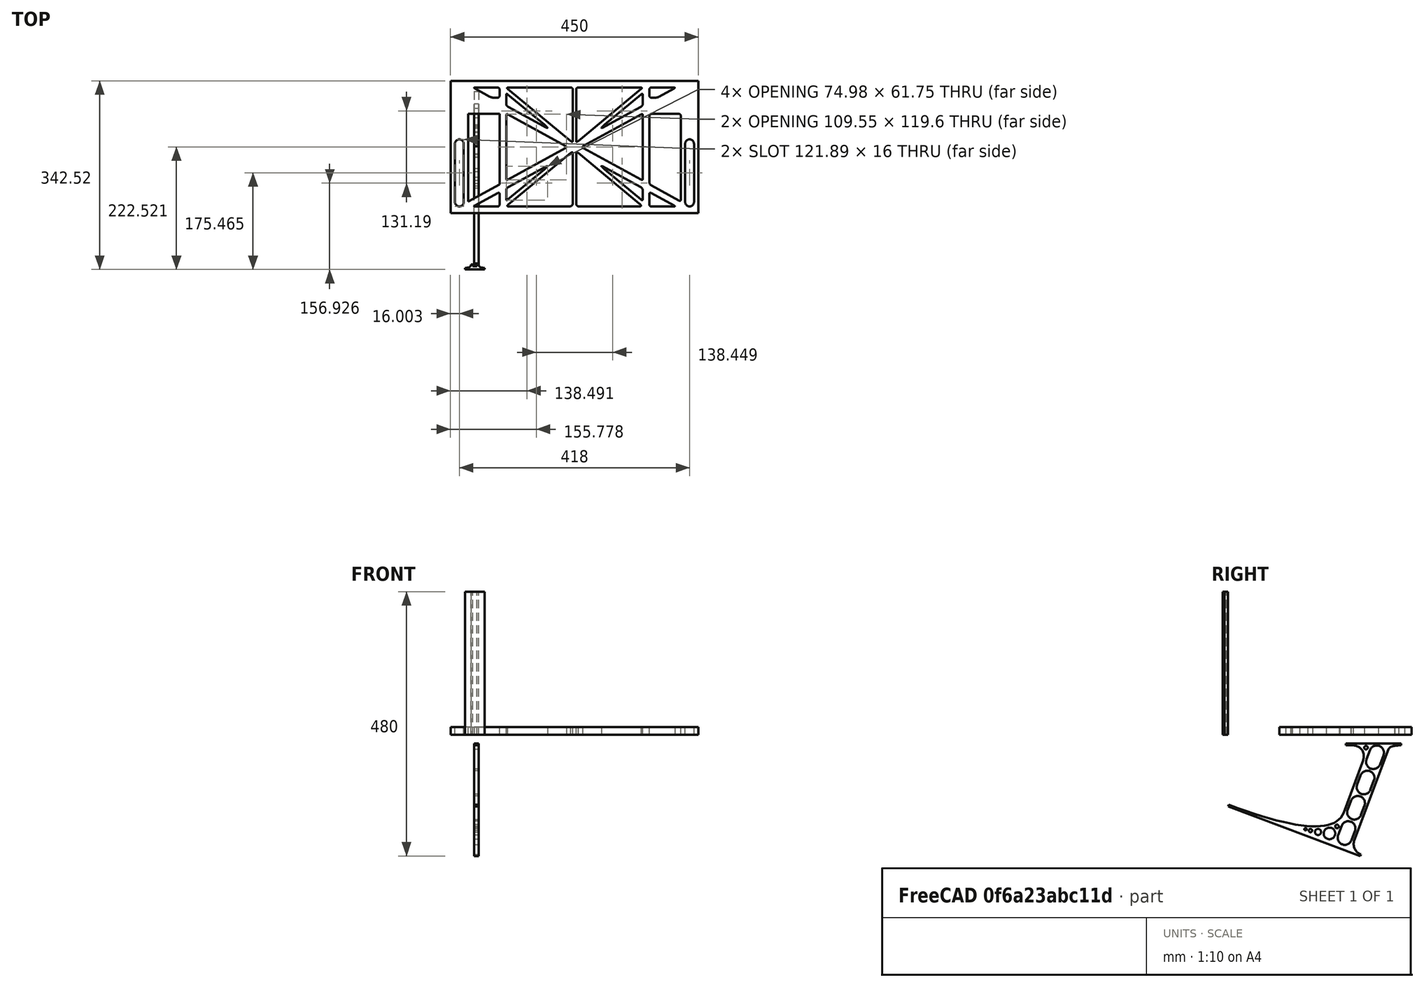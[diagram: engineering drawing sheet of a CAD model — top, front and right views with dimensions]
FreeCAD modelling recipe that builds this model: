
FCSTD DOCUMENT  (FreeCAD 0.19R0.19.2)
Label: laptopStand134FCStd
License: All rights reserved
LicenseURL: http://en.wikipedia.org/wiki/All_rights_reserved
objects: Sketcher::SketchObject×3, Part::Extrusion×3
note: 6 computed .brp shape members not serialized (recipe doc carries the construction recipe); baked Part::Feature solids carry a one-line shape summary decoded from their .brp

FEATURE [Sketcher::SketchObject] Sketch
  FullyConstrained = true
  sketch-geometry (349):
    g0: LineSegment StartX=-10.9272 StartY=-82.7794 StartZ=0 EndX=46.0728 EndY=-51.4823 EndZ=0
    g1: LineSegment StartX=-10.9272 StartY=76.4095 StartZ=0 EndX=-10.9272 EndY=-82.7794 EndZ=0
    g2: LineSegment StartX=46.0728 StartY=76.4095 StartZ=0 EndX=46.0728 EndY=-51.4823 EndZ=0
    g3: LineSegment StartX=-42.9272 StartY=136.221 StartZ=0 EndX=-42.9272 EndY=-103.779 EndZ=0
    g4: LineSegment StartX=407.073 StartY=136.221 StartZ=0 EndX=407.073 EndY=-103.779 EndZ=0
    g5: ArcOfCircle CenterX=-26.9272 CenterY=22.1087 CenterZ=0 NormalX=0 NormalY=0 NormalZ=1 AngleXU=0 Radius=8 StartAngle=1e-16 EndAngle=3.14159
    g6: ArcOfCircle CenterX=-26.9272 CenterY=-83.7794 CenterZ=0 NormalX=0 NormalY=0 NormalZ=1 AngleXU=0 Radius=8 StartAngle=3.14159 EndAngle=6.28319
    g7: LineSegment StartX=-34.9272 StartY=22.1087 StartZ=0 EndX=-34.9272 EndY=-83.7794 EndZ=0
    g8: LineSegment StartX=-18.9272 StartY=22.1087 StartZ=0 EndX=-18.9272 EndY=-83.7794 EndZ=0
    g9: ArcOfCircle CenterX=391.073 CenterY=22.1087 CenterZ=0 NormalX=0 NormalY=0 NormalZ=1 AngleXU=0 Radius=8 StartAngle=-4.4e-15 EndAngle=3.14159
    g10: LineSegment StartX=399.073 StartY=22.1087 StartZ=0 EndX=399.073 EndY=-83.7794 EndZ=0
    g11: LineSegment StartX=383.073 StartY=22.1087 StartZ=0 EndX=383.073 EndY=-83.7794 EndZ=0
    g12: ArcOfCircle CenterX=391.073 CenterY=-83.7794 CenterZ=0 NormalX=0 NormalY=0 NormalZ=1 AngleXU=0 Radius=8 StartAngle=3.14159 EndAngle=6.28319
    g13: Circle CenterX=175.022 CenterY=27.0628 CenterZ=0 NormalX=0 NormalY=0 NormalZ=1 AngleXU=0 Radius=1
    g14: Circle CenterX=179.022 CenterY=24.8665 CenterZ=0 NormalX=0 NormalY=0 NormalZ=1 AngleXU=0 Radius=1
    g15: Circle CenterX=179.022 CenterY=27.0628 CenterZ=0 NormalX=0 NormalY=0 NormalZ=1 AngleXU=0 Radius=1
    g16: BSplineCurve PolesCount=3 KnotsCount=2 Degree=2 IsPeriodic=0
    g17: GeomPoint X=175.022 Y=27.0628 Z=0
    g18: GeomPoint X=179.022 Y=27.0628 Z=0
    g19: Circle CenterX=189.124 CenterY=27.0628 CenterZ=0 NormalX=0 NormalY=0 NormalZ=1 AngleXU=0 Radius=1
    g20: Circle CenterX=185.124 CenterY=24.8665 CenterZ=0 NormalX=0 NormalY=0 NormalZ=1 AngleXU=0 Radius=1
    g21: Circle CenterX=185.124 CenterY=27.0628 CenterZ=0 NormalX=0 NormalY=0 NormalZ=1 AngleXU=0 Radius=1
    g22: BSplineCurve PolesCount=3 KnotsCount=2 Degree=2 IsPeriodic=0
    g23: GeomPoint X=189.124 Y=27.0628 Z=0
    g24: GeomPoint X=185.124 Y=27.0628 Z=0
    g25: Circle CenterX=175.022 CenterY=5.37834 CenterZ=0 NormalX=0 NormalY=0 NormalZ=1 AngleXU=0 Radius=1
    g26: Circle CenterX=179.022 CenterY=7.57463 CenterZ=0 NormalX=0 NormalY=0 NormalZ=1 AngleXU=0 Radius=1
    g27: Circle CenterX=179.022 CenterY=5.34704 CenterZ=0 NormalX=0 NormalY=0 NormalZ=1 AngleXU=0 Radius=1
    g28: BSplineCurve PolesCount=3 KnotsCount=2 Degree=2 IsPeriodic=0
    g29: GeomPoint X=175.022 Y=5.37834 Z=0
    g30: GeomPoint X=179.022 Y=5.34704 Z=0
    g31: Circle CenterX=189.124 CenterY=5.37834 CenterZ=0 NormalX=0 NormalY=0 NormalZ=1 AngleXU=0 Radius=1
    g32: Circle CenterX=185.124 CenterY=7.57463 CenterZ=0 NormalX=0 NormalY=0 NormalZ=1 AngleXU=0 Radius=1
    g33: Circle CenterX=185.124 CenterY=5.34704 CenterZ=0 NormalX=0 NormalY=0 NormalZ=1 AngleXU=0 Radius=1
    g34: BSplineCurve PolesCount=3 KnotsCount=2 Degree=2 IsPeriodic=0
    g35: GeomPoint X=189.124 Y=5.37834 Z=0
    g36: GeomPoint X=185.124 Y=5.34704 Z=0
    g37: Circle CenterX=165.871 CenterY=18.1458 CenterZ=0 NormalX=0 NormalY=0 NormalZ=1 AngleXU=0 Radius=1
    g38: Circle CenterX=169.377 CenterY=16.2206 CenterZ=0 NormalX=0 NormalY=0 NormalZ=1 AngleXU=0 Radius=1
    g39: Circle CenterX=165.871 CenterY=14.2954 CenterZ=0 NormalX=0 NormalY=0 NormalZ=1 AngleXU=0 Radius=1
    g40: BSplineCurve PolesCount=3 KnotsCount=2 Degree=2 IsPeriodic=0
    g41: GeomPoint X=165.871 Y=18.1458 Z=0
    g42: GeomPoint X=165.871 Y=14.2954 Z=0
    g43: Circle CenterX=198.275 CenterY=18.1458 CenterZ=0 NormalX=0 NormalY=0 NormalZ=1 AngleXU=0 Radius=1
    g44: Circle CenterX=194.768 CenterY=16.2206 CenterZ=0 NormalX=0 NormalY=0 NormalZ=1 AngleXU=0 Radius=1
    g45: Circle CenterX=198.275 CenterY=14.2954 CenterZ=0 NormalX=0 NormalY=0 NormalZ=1 AngleXU=0 Radius=1
    g46: BSplineCurve PolesCount=3 KnotsCount=2 Degree=2 IsPeriodic=0
    g47: GeomPoint X=198.275 Y=18.1458 Z=0
    g48: GeomPoint X=198.275 Y=14.2954 Z=0
    g49: LineSegment StartX=407.073 StartY=-103.779 StartZ=0 EndX=-42.9272 EndY=-103.779 EndZ=0
    g50: LineSegment StartX=407.073 StartY=136.221 StartZ=0 EndX=-42.9272 EndY=136.221 EndZ=0
    g51: LineSegment StartX=46.0728 StartY=76.4095 StartZ=0 EndX=-10.9272 EndY=76.4095 EndZ=0
    g52: Circle CenterX=125.607 CenterY=54.1951 CenterZ=0 NormalX=0 NormalY=0 NormalZ=1 AngleXU=0 Radius=1
    g53: Circle CenterX=139.632 CenterY=46.4944 CenterZ=0 NormalX=0 NormalY=0 NormalZ=1 AngleXU=0 Radius=1
    g54: Circle CenterX=127.326 CenterY=56.7187 CenterZ=0 NormalX=0 NormalY=0 NormalZ=1 AngleXU=0 Radius=1
    g55: BSplineCurve PolesCount=3 KnotsCount=2 Degree=2 IsPeriodic=0
    g56: GeomPoint X=125.607 Y=54.1951 Z=0
    g57: GeomPoint X=127.326 Y=56.7187 Z=0
    g58: Circle CenterX=236.821 CenterY=56.7187 CenterZ=0 NormalX=0 NormalY=0 NormalZ=1 AngleXU=0 Radius=1
    g59: Circle CenterX=224.513 CenterY=46.4944 CenterZ=0 NormalX=0 NormalY=0 NormalZ=1 AngleXU=0 Radius=1
    g60: Circle CenterX=238.538 CenterY=54.1951 CenterZ=0 NormalX=0 NormalY=0 NormalZ=1 AngleXU=0 Radius=1
    g61: BSplineCurve PolesCount=3 KnotsCount=2 Degree=2 IsPeriodic=0
    g62: GeomPoint X=236.821 Y=56.7187 Z=0
    g63: GeomPoint X=238.538 Y=54.1951 Z=0
    g64: Circle CenterX=238.538 CenterY=-21.7539 CenterZ=0 NormalX=0 NormalY=0 NormalZ=1 AngleXU=0 Radius=1
    g65: Circle CenterX=224.513 CenterY=-14.0532 CenterZ=0 NormalX=0 NormalY=0 NormalZ=1 AngleXU=0 Radius=1
    g66: Circle CenterX=236.821 CenterY=-24.2775 CenterZ=0 NormalX=0 NormalY=0 NormalZ=1 AngleXU=0 Radius=1
    g67: BSplineCurve PolesCount=3 KnotsCount=2 Degree=2 IsPeriodic=0
    g68: GeomPoint X=238.538 Y=-21.7539 Z=0
    g69: GeomPoint X=236.821 Y=-24.2775 Z=0
    g70: Circle CenterX=125.607 CenterY=-21.7539 CenterZ=0 NormalX=0 NormalY=0 NormalZ=1 AngleXU=0 Radius=1
    g71: Circle CenterX=139.632 CenterY=-14.0532 CenterZ=0 NormalX=0 NormalY=0 NormalZ=1 AngleXU=0 Radius=1
    g72: Circle CenterX=127.325 CenterY=-24.2775 CenterZ=0 NormalX=0 NormalY=0 NormalZ=1 AngleXU=0 Radius=1
    g73: BSplineCurve PolesCount=3 KnotsCount=2 Degree=2 IsPeriodic=0
    g74: GeomPoint X=125.607 Y=-21.7539 Z=0
    g75: GeomPoint X=127.325 Y=-24.2775 Z=0
    g76: Circle CenterX=302.996 CenterY=111.695 CenterZ=0 NormalX=0 NormalY=0 NormalZ=1 AngleXU=0 Radius=1
    g77: Circle CenterX=306.073 CenterY=114.251 CenterZ=0 NormalX=0 NormalY=0 NormalZ=1 AngleXU=0 Radius=1
    g78: Circle CenterX=306.073 CenterY=110.251 CenterZ=0 NormalX=0 NormalY=0 NormalZ=1 AngleXU=0 Radius=1
    g79: BSplineCurve PolesCount=3 KnotsCount=2 Degree=2 IsPeriodic=0
    g80: GeomPoint X=302.996 Y=111.695 Z=0
    g81: GeomPoint X=306.073 Y=110.251 Z=0
    g82: Circle CenterX=306.073 CenterY=95.2763 CenterZ=0 NormalX=0 NormalY=0 NormalZ=1 AngleXU=0 Radius=1
    g83: Circle CenterX=306.073 CenterY=91.2763 CenterZ=0 NormalX=0 NormalY=0 NormalZ=1 AngleXU=0 Radius=1
    g84: Circle CenterX=302.567 CenterY=89.3511 CenterZ=0 NormalX=0 NormalY=0 NormalZ=1 AngleXU=0 Radius=1
    g85: BSplineCurve PolesCount=3 KnotsCount=2 Degree=2 IsPeriodic=0
    g86: GeomPoint X=306.073 Y=95.2763 Z=0
    g87: GeomPoint X=302.567 Y=89.3511 Z=0
    g88: LineSegment StartX=306.073 StartY=110.251 StartZ=0 EndX=306.073 EndY=95.2763 EndZ=0
    g89: LineSegment StartX=302.996 StartY=111.695 StartZ=0 EndX=236.821 EndY=56.7187 EndZ=0
    g90: LineSegment StartX=238.538 StartY=54.1951 StartZ=0 EndX=302.567 EndY=89.3511 EndZ=0
    g91: Circle CenterX=61.1496 CenterY=111.695 CenterZ=0 NormalX=0 NormalY=0 NormalZ=1 AngleXU=0 Radius=1
    g92: Circle CenterX=58.0728 CenterY=114.251 CenterZ=0 NormalX=0 NormalY=0 NormalZ=1 AngleXU=0 Radius=1
    g93: Circle CenterX=58.0728 CenterY=110.251 CenterZ=0 NormalX=0 NormalY=0 NormalZ=1 AngleXU=0 Radius=1
    g94: BSplineCurve PolesCount=3 KnotsCount=2 Degree=2 IsPeriodic=0
    g95: GeomPoint X=61.1496 Y=111.695 Z=0
    g96: GeomPoint X=58.0728 Y=110.251 Z=0
    g97: Circle CenterX=61.5791 CenterY=89.3511 CenterZ=0 NormalX=0 NormalY=0 NormalZ=1 AngleXU=0 Radius=1
    g98: Circle CenterX=58.0728 CenterY=91.2763 CenterZ=0 NormalX=0 NormalY=0 NormalZ=1 AngleXU=0 Radius=1
    g99: Circle CenterX=58.0728 CenterY=95.2763 CenterZ=0 NormalX=0 NormalY=0 NormalZ=1 AngleXU=0 Radius=1
    g100: BSplineCurve PolesCount=3 KnotsCount=2 Degree=2 IsPeriodic=0
    g101: GeomPoint X=61.5791 Y=89.3511 Z=0
    g102: GeomPoint X=58.0728 Y=95.2763 Z=0
    g103: LineSegment StartX=58.0728 StartY=110.251 StartZ=0 EndX=58.0728 EndY=95.2763 EndZ=0
    g104: LineSegment StartX=61.1496 StartY=111.695 StartZ=0 EndX=127.326 EndY=56.7187 EndZ=0
    g105: LineSegment StartX=125.607 StartY=54.1951 StartZ=0 EndX=61.5791 EndY=89.3511 EndZ=0
    g106: Circle CenterX=61.5791 CenterY=-56.9099 CenterZ=0 NormalX=0 NormalY=0 NormalZ=1 AngleXU=0 Radius=1
    g107: Circle CenterX=58.0728 CenterY=-58.8351 CenterZ=0 NormalX=0 NormalY=0 NormalZ=1 AngleXU=0 Radius=1
    g108: Circle CenterX=58.0728 CenterY=-62.8351 CenterZ=0 NormalX=0 NormalY=0 NormalZ=1 AngleXU=0 Radius=1
    g109: BSplineCurve PolesCount=3 KnotsCount=2 Degree=2 IsPeriodic=0
    g110: GeomPoint X=61.5791 Y=-56.9099 Z=0
    g111: GeomPoint X=58.0728 Y=-62.8351 Z=0
    g112: Circle CenterX=58.0728 CenterY=-77.8102 CenterZ=0 NormalX=0 NormalY=0 NormalZ=1 AngleXU=0 Radius=1
    g113: Circle CenterX=58.0728 CenterY=-81.8102 CenterZ=0 NormalX=0 NormalY=0 NormalZ=1 AngleXU=0 Radius=1
    g114: Circle CenterX=61.1496 CenterY=-79.2541 CenterZ=0 NormalX=0 NormalY=0 NormalZ=1 AngleXU=0 Radius=1
    g115: BSplineCurve PolesCount=3 KnotsCount=2 Degree=2 IsPeriodic=0
    g116: GeomPoint X=58.0728 Y=-77.8102 Z=0
    g117: GeomPoint X=61.1496 Y=-79.2541 Z=0
    g118: LineSegment StartX=58.0728 StartY=-62.8351 StartZ=0 EndX=58.0728 EndY=-77.8102 EndZ=0
    g119: LineSegment StartX=61.1496 StartY=-79.2541 StartZ=0 EndX=127.325 EndY=-24.2775 EndZ=0
    g120: LineSegment StartX=125.607 StartY=-21.7539 StartZ=0 EndX=61.5791 EndY=-56.9099 EndZ=0
    g121: Circle CenterX=302.567 CenterY=-56.9099 CenterZ=0 NormalX=0 NormalY=0 NormalZ=1 AngleXU=0 Radius=1
    g122: Circle CenterX=306.073 CenterY=-58.8351 CenterZ=0 NormalX=0 NormalY=0 NormalZ=1 AngleXU=0 Radius=1
    g123: Circle CenterX=306.073 CenterY=-62.8351 CenterZ=0 NormalX=0 NormalY=0 NormalZ=1 AngleXU=0 Radius=1
    g124: BSplineCurve PolesCount=3 KnotsCount=2 Degree=2 IsPeriodic=0
    g125: GeomPoint X=302.567 Y=-56.9099 Z=0
    g126: GeomPoint X=306.073 Y=-62.8351 Z=0
    g127: Circle CenterX=302.996 CenterY=-79.2541 CenterZ=0 NormalX=0 NormalY=0 NormalZ=1 AngleXU=0 Radius=1
    g128: Circle CenterX=306.073 CenterY=-81.8102 CenterZ=0 NormalX=0 NormalY=0 NormalZ=1 AngleXU=0 Radius=1
    g129: Circle CenterX=306.073 CenterY=-77.8102 CenterZ=0 NormalX=0 NormalY=0 NormalZ=1 AngleXU=0 Radius=1
    g130: BSplineCurve PolesCount=3 KnotsCount=2 Degree=2 IsPeriodic=0
    g131: GeomPoint X=302.996 Y=-79.2541 Z=0
    g132: GeomPoint X=306.073 Y=-77.8102 Z=0
    g133: LineSegment StartX=306.073 StartY=-62.8351 StartZ=0 EndX=306.073 EndY=-77.8102 EndZ=0
    g134: LineSegment StartX=302.996 StartY=-79.2541 StartZ=0 EndX=236.821 EndY=-24.2775 EndZ=0
    g135: LineSegment StartX=238.538 StartY=-21.7539 StartZ=0 EndX=302.567 EndY=-56.9099 EndZ=0
    g136: Circle CenterX=61.6457 CenterY=-88.8112 CenterZ=0 NormalX=0 NormalY=0 NormalZ=1 AngleXU=0 Radius=1
    g137: Circle CenterX=58.0728 CenterY=-91.7794 CenterZ=0 NormalX=0 NormalY=0 NormalZ=1 AngleXU=0 Radius=1
    g138: Circle CenterX=63.9135 CenterY=-91.7794 CenterZ=0 NormalX=0 NormalY=0 NormalZ=1 AngleXU=0 Radius=1
    g139: BSplineCurve PolesCount=3 KnotsCount=2 Degree=2 IsPeriodic=0
    g140: GeomPoint X=61.6457 Y=-88.8112 Z=0
    g141: GeomPoint X=63.9135 Y=-91.7794 Z=0
    g142: Circle CenterX=179.022 CenterY=-85.8163 CenterZ=0 NormalX=0 NormalY=0 NormalZ=1 AngleXU=0 Radius=1
    g143: Circle CenterX=179.022 CenterY=-91.7794 CenterZ=0 NormalX=0 NormalY=0 NormalZ=1 AngleXU=0 Radius=1
    g144: Circle CenterX=171.895 CenterY=-91.7794 CenterZ=0 NormalX=0 NormalY=0 NormalZ=1 AngleXU=0 Radius=1
    g145: BSplineCurve PolesCount=3 KnotsCount=2 Degree=2 IsPeriodic=0
    g146: GeomPoint X=179.022 Y=-85.8163 Z=0
    g147: GeomPoint X=171.895 Y=-91.7794 Z=0
    g148: Circle CenterX=185.124 CenterY=-86.2028 CenterZ=0 NormalX=0 NormalY=0 NormalZ=1 AngleXU=0 Radius=1
    g149: Circle CenterX=185.124 CenterY=-91.7794 CenterZ=0 NormalX=0 NormalY=0 NormalZ=1 AngleXU=0 Radius=1
    g150: Circle CenterX=191.747 CenterY=-91.7794 CenterZ=0 NormalX=0 NormalY=0 NormalZ=1 AngleXU=0 Radius=1
    g151: BSplineCurve PolesCount=3 KnotsCount=2 Degree=2 IsPeriodic=0
    g152: GeomPoint X=185.124 Y=-86.2028 Z=0
    g153: GeomPoint X=191.747 Y=-91.7794 Z=0
    g154: Circle CenterX=299.888 CenterY=-86.6413 CenterZ=0 NormalX=0 NormalY=0 NormalZ=1 AngleXU=0 Radius=1
    g155: Circle CenterX=306.073 CenterY=-91.7794 CenterZ=0 NormalX=0 NormalY=0 NormalZ=1 AngleXU=0 Radius=1
    g156: Circle CenterX=298.776 CenterY=-91.7794 CenterZ=0 NormalX=0 NormalY=0 NormalZ=1 AngleXU=0 Radius=1
    g157: BSplineCurve PolesCount=3 KnotsCount=2 Degree=2 IsPeriodic=0
    g158: GeomPoint X=299.888 Y=-86.6413 Z=0
    g159: GeomPoint X=298.776 Y=-91.7794 Z=0
    g160: LineSegment StartX=189.124 StartY=5.37834 StartZ=0 EndX=299.888 EndY=-86.6413 EndZ=0
    g161: LineSegment StartX=298.776 StartY=-91.7794 StartZ=0 EndX=191.747 EndY=-91.7794 EndZ=0
    g162: LineSegment StartX=185.124 StartY=-86.2028 StartZ=0 EndX=185.124 EndY=5.34704 EndZ=0
    g163: LineSegment StartX=179.022 StartY=5.34704 StartZ=0 EndX=179.022 EndY=-85.8163 EndZ=0
    g164: LineSegment StartX=171.895 StartY=-91.7794 StartZ=0 EndX=63.9135 EndY=-91.7794 EndZ=0
    g165: LineSegment StartX=61.6457 StartY=-88.8112 StartZ=0 EndX=175.022 EndY=5.37834 EndZ=0
    g166: Circle CenterX=302.073 CenterY=124.221 CenterZ=0 NormalX=0 NormalY=0 NormalZ=1 AngleXU=0 Radius=1
    g167: Circle CenterX=306.073 CenterY=124.221 CenterZ=0 NormalX=0 NormalY=0 NormalZ=1 AngleXU=0 Radius=1
    g168: Circle CenterX=302.996 CenterY=121.665 CenterZ=0 NormalX=0 NormalY=0 NormalZ=1 AngleXU=0 Radius=1
    g169: BSplineCurve PolesCount=3 KnotsCount=2 Degree=2 IsPeriodic=0
    g170: GeomPoint X=302.073 Y=124.221 Z=0
    g171: GeomPoint X=302.996 Y=121.665 Z=0
    g172: Circle CenterX=189.124 CenterY=124.221 CenterZ=0 NormalX=0 NormalY=0 NormalZ=1 AngleXU=0 Radius=1
    g173: Circle CenterX=185.124 CenterY=124.221 CenterZ=0 NormalX=0 NormalY=0 NormalZ=1 AngleXU=0 Radius=1
    g174: Circle CenterX=185.124 CenterY=120.221 CenterZ=0 NormalX=0 NormalY=0 NormalZ=1 AngleXU=0 Radius=1
    g175: BSplineCurve PolesCount=3 KnotsCount=2 Degree=2 IsPeriodic=0
    g176: GeomPoint X=189.124 Y=124.221 Z=0
    g177: GeomPoint X=185.124 Y=120.221 Z=0
    g178: Circle CenterX=175.022 CenterY=124.221 CenterZ=0 NormalX=0 NormalY=0 NormalZ=1 AngleXU=0 Radius=1
    g179: Circle CenterX=179.022 CenterY=124.221 CenterZ=0 NormalX=0 NormalY=0 NormalZ=1 AngleXU=0 Radius=1
    g180: Circle CenterX=179.022 CenterY=120.221 CenterZ=0 NormalX=0 NormalY=0 NormalZ=1 AngleXU=0 Radius=1
    g181: BSplineCurve PolesCount=3 KnotsCount=2 Degree=2 IsPeriodic=0
    g182: GeomPoint X=175.022 Y=124.221 Z=0
    g183: GeomPoint X=179.022 Y=120.221 Z=0
    g184: Circle CenterX=62.0728 CenterY=124.221 CenterZ=0 NormalX=0 NormalY=0 NormalZ=1 AngleXU=0 Radius=1
    g185: Circle CenterX=58.0728 CenterY=124.221 CenterZ=0 NormalX=0 NormalY=0 NormalZ=1 AngleXU=0 Radius=1
    g186: Circle CenterX=61.1496 CenterY=121.665 CenterZ=0 NormalX=0 NormalY=0 NormalZ=1 AngleXU=0 Radius=1
    g187: BSplineCurve PolesCount=3 KnotsCount=2 Degree=2 IsPeriodic=0
    g188: GeomPoint X=62.0728 Y=124.221 Z=0
    g189: GeomPoint X=61.1496 Y=121.665 Z=0
    g190: LineSegment StartX=62.0728 StartY=124.221 StartZ=0 EndX=175.022 EndY=124.221 EndZ=0
    g191: LineSegment StartX=179.022 StartY=120.221 StartZ=0 EndX=179.022 EndY=27.0628 EndZ=0
    g192: LineSegment StartX=185.124 StartY=27.0628 StartZ=0 EndX=185.124 EndY=120.221 EndZ=0
    g193: LineSegment StartX=189.124 StartY=124.221 StartZ=0 EndX=302.073 EndY=124.221 EndZ=0
    g194: LineSegment StartX=302.996 StartY=121.665 StartZ=0 EndX=189.124 EndY=27.0628 EndZ=0
    g195: LineSegment StartX=175.022 StartY=27.0628 StartZ=0 EndX=61.1496 EndY=121.665 EndZ=0
    g196: Circle CenterX=61.5791 CenterY=75.4095 CenterZ=0 NormalX=0 NormalY=0 NormalZ=1 AngleXU=0 Radius=1
    g197: Circle CenterX=58.0728 CenterY=77.3346 CenterZ=0 NormalX=0 NormalY=0 NormalZ=1 AngleXU=0 Radius=1
    g198: Circle CenterX=58.0728 CenterY=73.3346 CenterZ=0 NormalX=0 NormalY=0 NormalZ=1 AngleXU=0 Radius=1
    g199: BSplineCurve PolesCount=3 KnotsCount=2 Degree=2 IsPeriodic=0
    g200: GeomPoint X=61.5791 Y=75.4095 Z=0
    g201: GeomPoint X=58.0728 Y=73.3346 Z=0
    g202: Circle CenterX=58.0728 CenterY=-40.8935 CenterZ=0 NormalX=0 NormalY=0 NormalZ=1 AngleXU=0 Radius=1
    g203: Circle CenterX=58.0728 CenterY=-44.8935 CenterZ=0 NormalX=0 NormalY=0 NormalZ=1 AngleXU=0 Radius=1
    g204: Circle CenterX=61.5791 CenterY=-42.9683 CenterZ=0 NormalX=0 NormalY=0 NormalZ=1 AngleXU=0 Radius=1
    g205: BSplineCurve PolesCount=3 KnotsCount=2 Degree=2 IsPeriodic=0
    g206: GeomPoint X=58.0728 Y=-40.8935 Z=0
    g207: GeomPoint X=61.5791 Y=-42.9683 Z=0
    g208: LineSegment StartX=61.5791 StartY=-42.9683 StartZ=0 EndX=165.871 EndY=14.2954 EndZ=0
    g209: LineSegment StartX=165.871 StartY=18.1458 StartZ=0 EndX=61.5791 EndY=75.4095 EndZ=0
    g210: LineSegment StartX=58.0728 StartY=73.3346 StartZ=0 EndX=58.0728 EndY=-40.8935 EndZ=0
    g211: Circle CenterX=302.567 CenterY=-42.9683 CenterZ=0 NormalX=0 NormalY=0 NormalZ=1 AngleXU=0 Radius=1
    g212: Circle CenterX=306.073 CenterY=-44.8935 CenterZ=0 NormalX=0 NormalY=0 NormalZ=1 AngleXU=0 Radius=1
    g213: Circle CenterX=306.073 CenterY=-40.8935 CenterZ=0 NormalX=0 NormalY=0 NormalZ=1 AngleXU=0 Radius=1
    g214: BSplineCurve PolesCount=3 KnotsCount=2 Degree=2 IsPeriodic=0
    g215: GeomPoint X=302.567 Y=-42.9683 Z=0
    g216: GeomPoint X=306.073 Y=-40.8935 Z=0
    g217: Circle CenterX=306.073 CenterY=73.3346 CenterZ=0 NormalX=0 NormalY=0 NormalZ=1 AngleXU=0 Radius=1
    g218: Circle CenterX=306.073 CenterY=77.3346 CenterZ=0 NormalX=0 NormalY=0 NormalZ=1 AngleXU=0 Radius=1
    g219: Circle CenterX=302.567 CenterY=75.4095 CenterZ=0 NormalX=0 NormalY=0 NormalZ=1 AngleXU=0 Radius=1
    g220: BSplineCurve PolesCount=3 KnotsCount=2 Degree=2 IsPeriodic=0
    g221: GeomPoint X=306.073 Y=73.3346 Z=0
    g222: GeomPoint X=302.567 Y=75.4095 Z=0
    g223: LineSegment StartX=302.567 StartY=-42.9683 StartZ=0 EndX=198.275 EndY=14.2954 EndZ=0
    g224: LineSegment StartX=198.275 StartY=18.1458 StartZ=0 EndX=302.567 EndY=75.4095 EndZ=0
    g225: LineSegment StartX=306.073 StartY=73.3346 StartZ=0 EndX=306.073 EndY=-40.8935 EndZ=0
    g226: LineSegment StartX=322.073 StartY=105.865 StartZ=0 EndX=328.643 EndY=105.865 EndZ=0
    g227: LineSegment StartX=318.073 StartY=120.221 StartZ=0 EndX=318.073 EndY=109.865 EndZ=0
    g228: LineSegment StartX=336.157 StartY=107.779 StartZ=0 EndX=362.567 EndY=122.294 EndZ=0
    g229: Circle CenterX=362.073 CenterY=124.221 CenterZ=0 NormalX=0 NormalY=0 NormalZ=1 AngleXU=0 Radius=1
    g230: Circle CenterX=366.073 CenterY=124.221 CenterZ=0 NormalX=0 NormalY=0 NormalZ=1 AngleXU=0 Radius=1
    g231: Circle CenterX=362.567 CenterY=122.294 CenterZ=0 NormalX=0 NormalY=0 NormalZ=1 AngleXU=0 Radius=1
    g232: BSplineCurve PolesCount=3 KnotsCount=2 Degree=2 IsPeriodic=0
    g233: GeomPoint X=362.073 Y=124.221 Z=0
    g234: GeomPoint X=362.567 Y=122.294 Z=0
    g235: Circle CenterX=322.073 CenterY=124.221 CenterZ=0 NormalX=0 NormalY=0 NormalZ=1 AngleXU=0 Radius=1
    g236: Circle CenterX=318.073 CenterY=124.221 CenterZ=0 NormalX=0 NormalY=0 NormalZ=1 AngleXU=0 Radius=1
    g237: Circle CenterX=318.073 CenterY=120.221 CenterZ=0 NormalX=0 NormalY=0 NormalZ=1 AngleXU=0 Radius=1
    g238: BSplineCurve PolesCount=3 KnotsCount=2 Degree=2 IsPeriodic=0
    g239: GeomPoint X=322.073 Y=124.221 Z=0
    g240: GeomPoint X=318.073 Y=120.221 Z=0
    g241: Circle CenterX=322.073 CenterY=105.865 CenterZ=0 NormalX=0 NormalY=0 NormalZ=1 AngleXU=0 Radius=1
    g242: Circle CenterX=318.073 CenterY=105.865 CenterZ=0 NormalX=0 NormalY=0 NormalZ=1 AngleXU=0 Radius=1
    g243: Circle CenterX=318.073 CenterY=109.865 CenterZ=0 NormalX=0 NormalY=0 NormalZ=1 AngleXU=0 Radius=1
    g244: BSplineCurve PolesCount=3 KnotsCount=2 Degree=2 IsPeriodic=0
    g245: GeomPoint X=322.073 Y=105.865 Z=0
    g246: GeomPoint X=318.073 Y=109.865 Z=0
    g247: Circle CenterX=336.157 CenterY=107.779 CenterZ=0 NormalX=0 NormalY=0 NormalZ=1 AngleXU=0 Radius=1
    g248: Circle CenterX=332.651 CenterY=105.853 CenterZ=0 NormalX=0 NormalY=0 NormalZ=1 AngleXU=0 Radius=1
    g249: Circle CenterX=328.643 CenterY=105.865 CenterZ=0 NormalX=0 NormalY=0 NormalZ=1 AngleXU=0 Radius=1
    g250: BSplineCurve PolesCount=3 KnotsCount=2 Degree=2 IsPeriodic=0
    g251: GeomPoint X=336.157 Y=107.779 Z=0
    g252: GeomPoint X=328.643 Y=105.865 Z=0
    g253: LineSegment StartX=322.073 StartY=124.221 StartZ=0 EndX=362.073 EndY=124.221 EndZ=0
    g254: Circle CenterX=371.567 CenterY=-80.8644 CenterZ=0 NormalX=0 NormalY=0 NormalZ=1 AngleXU=0 Radius=1
    g255: Circle CenterX=375.073 CenterY=-82.7896 CenterZ=0 NormalX=0 NormalY=0 NormalZ=1 AngleXU=0 Radius=1
    g256: Circle CenterX=375.073 CenterY=-78.7896 CenterZ=0 NormalX=0 NormalY=0 NormalZ=1 AngleXU=0 Radius=1
    g257: BSplineCurve PolesCount=3 KnotsCount=2 Degree=2 IsPeriodic=0
    g258: GeomPoint X=371.567 Y=-80.8644 Z=0
    g259: GeomPoint X=375.073 Y=-78.7896 Z=0
    g260: Circle CenterX=321.579 CenterY=-53.4075 CenterZ=0 NormalX=0 NormalY=0 NormalZ=1 AngleXU=0 Radius=1
    g261: Circle CenterX=318.073 CenterY=-51.4823 CenterZ=0 NormalX=0 NormalY=0 NormalZ=1 AngleXU=0 Radius=1
    g262: Circle CenterX=318.073 CenterY=-47.4823 CenterZ=0 NormalX=0 NormalY=0 NormalZ=1 AngleXU=0 Radius=1
    g263: BSplineCurve PolesCount=3 KnotsCount=2 Degree=2 IsPeriodic=0
    g264: GeomPoint X=321.579 Y=-53.4075 Z=0
    g265: GeomPoint X=318.073 Y=-47.4823 Z=0
    g266: LineSegment StartX=371.567 StartY=-80.8644 StartZ=0 EndX=321.579 EndY=-53.4075 EndZ=0
    g267: Circle CenterX=321.579 CenterY=-67.3492 CenterZ=0 NormalX=0 NormalY=0 NormalZ=1 AngleXU=0 Radius=1
    g268: Circle CenterX=318.073 CenterY=-65.424 CenterZ=0 NormalX=0 NormalY=0 NormalZ=1 AngleXU=0 Radius=1
    g269: Circle CenterX=318.073 CenterY=-69.424 CenterZ=0 NormalX=0 NormalY=0 NormalZ=1 AngleXU=0 Radius=1
    g270: BSplineCurve PolesCount=3 KnotsCount=2 Degree=2 IsPeriodic=0
    g271: GeomPoint X=321.579 Y=-67.3492 Z=0
    g272: GeomPoint X=318.073 Y=-69.424 Z=0
    g273: Circle CenterX=362.567 CenterY=-89.8542 CenterZ=0 NormalX=0 NormalY=0 NormalZ=1 AngleXU=0 Radius=1
    g274: Circle CenterX=366.073 CenterY=-91.7794 CenterZ=0 NormalX=0 NormalY=0 NormalZ=1 AngleXU=0 Radius=1
    g275: Circle CenterX=362.073 CenterY=-91.7794 CenterZ=0 NormalX=0 NormalY=0 NormalZ=1 AngleXU=0 Radius=1
    g276: BSplineCurve PolesCount=3 KnotsCount=2 Degree=2 IsPeriodic=0
    g277: GeomPoint X=362.567 Y=-89.8542 Z=0
    g278: GeomPoint X=362.073 Y=-91.7794 Z=0
    g279: Circle CenterX=322.073 CenterY=-91.7794 CenterZ=0 NormalX=0 NormalY=0 NormalZ=1 AngleXU=0 Radius=1
    g280: Circle CenterX=318.073 CenterY=-91.7794 CenterZ=0 NormalX=0 NormalY=0 NormalZ=1 AngleXU=0 Radius=1
    g281: Circle CenterX=318.073 CenterY=-87.7794 CenterZ=0 NormalX=0 NormalY=0 NormalZ=1 AngleXU=0 Radius=1
    g282: BSplineCurve PolesCount=3 KnotsCount=2 Degree=2 IsPeriodic=0
    g283: GeomPoint X=322.073 Y=-91.7794 Z=0
    g284: GeomPoint X=318.073 Y=-87.7794 Z=0
    g285: LineSegment StartX=362.567 StartY=-89.8542 StartZ=0 EndX=321.579 EndY=-67.3492 EndZ=0
    g286: LineSegment StartX=318.073 StartY=-69.424 StartZ=0 EndX=318.073 EndY=-87.7794 EndZ=0
    g287: LineSegment StartX=322.073 StartY=-91.7794 StartZ=0 EndX=362.073 EndY=-91.7794 EndZ=0
    g288: Circle CenterX=2.07281 CenterY=124.221 CenterZ=0 NormalX=0 NormalY=0 NormalZ=1 AngleXU=0 Radius=1
    g289: Circle CenterX=1.57905 CenterY=122.295 CenterZ=0 NormalX=0 NormalY=0 NormalZ=1 AngleXU=0 Radius=1
    g290: BSplineCurve PolesCount=3 KnotsCount=2 Degree=2 IsPeriodic=0
    g291: GeomPoint X=2.07281 Y=124.221 Z=0
    g292: GeomPoint X=1.57905 Y=122.295 Z=0
    g293: Circle CenterX=42.0728 CenterY=124.221 CenterZ=0 NormalX=0 NormalY=0 NormalZ=1 AngleXU=0 Radius=1
    g294: Circle CenterX=46.0728 CenterY=124.221 CenterZ=0 NormalX=0 NormalY=0 NormalZ=1 AngleXU=0 Radius=1
    g295: Circle CenterX=46.0728 CenterY=120.221 CenterZ=0 NormalX=0 NormalY=0 NormalZ=1 AngleXU=0 Radius=1
    g296: BSplineCurve PolesCount=3 KnotsCount=2 Degree=2 IsPeriodic=0
    g297: GeomPoint X=42.0728 Y=124.221 Z=0
    g298: GeomPoint X=46.0728 Y=120.221 Z=0
    g299: Circle CenterX=46.0728 CenterY=109.865 CenterZ=0 NormalX=0 NormalY=0 NormalZ=1 AngleXU=0 Radius=1
    g300: Circle CenterX=46.0728 CenterY=105.865 CenterZ=0 NormalX=0 NormalY=0 NormalZ=1 AngleXU=0 Radius=1
    g301: Circle CenterX=42.0728 CenterY=105.865 CenterZ=0 NormalX=0 NormalY=0 NormalZ=1 AngleXU=0 Radius=1
    g302: BSplineCurve PolesCount=3 KnotsCount=2 Degree=2 IsPeriodic=0
    g303: GeomPoint X=46.0728 Y=109.865 Z=0
    g304: GeomPoint X=42.0728 Y=105.865 Z=0
    g305: Circle CenterX=35.5028 CenterY=105.865 CenterZ=0 NormalX=0 NormalY=0 NormalZ=1 AngleXU=0 Radius=1
    g306: Circle CenterX=31.5028 CenterY=105.865 CenterZ=0 NormalX=0 NormalY=0 NormalZ=1 AngleXU=0 Radius=1
    g307: Circle CenterX=27.9965 CenterY=107.79 CenterZ=0 NormalX=0 NormalY=0 NormalZ=1 AngleXU=0 Radius=1
    g308: BSplineCurve PolesCount=3 KnotsCount=2 Degree=2 IsPeriodic=0
    g309: GeomPoint X=35.5028 Y=105.865 Z=0
    g310: GeomPoint X=27.9965 Y=107.79 Z=0
    g311: LineSegment StartX=2.07281 StartY=124.221 StartZ=0 EndX=42.0728 EndY=124.221 EndZ=0
    g312: LineSegment StartX=46.0728 StartY=120.221 StartZ=0 EndX=46.0728 EndY=109.865 EndZ=0
    g313: LineSegment StartX=42.0728 StartY=105.865 StartZ=0 EndX=35.5028 EndY=105.865 EndZ=0
    g314: LineSegment StartX=27.9965 StartY=107.79 StartZ=0 EndX=1.57905 EndY=122.295 EndZ=0
    g315: Circle CenterX=42.5666 CenterY=-67.3492 CenterZ=0 NormalX=0 NormalY=0 NormalZ=1 AngleXU=0 Radius=1
    g316: Circle CenterX=46.0728 CenterY=-65.424 CenterZ=0 NormalX=0 NormalY=0 NormalZ=1 AngleXU=0 Radius=1
    g317: Circle CenterX=46.0728 CenterY=-69.424 CenterZ=0 NormalX=0 NormalY=0 NormalZ=1 AngleXU=0 Radius=1
    g318: BSplineCurve PolesCount=3 KnotsCount=2 Degree=2 IsPeriodic=0
    g319: GeomPoint X=42.5666 Y=-67.3492 Z=0
    g320: GeomPoint X=46.0728 Y=-69.424 Z=0
    g321: Circle CenterX=46.0728 CenterY=-87.7794 CenterZ=0 NormalX=0 NormalY=0 NormalZ=1 AngleXU=0 Radius=1
    g322: Circle CenterX=46.0728 CenterY=-91.7794 CenterZ=0 NormalX=0 NormalY=0 NormalZ=1 AngleXU=0 Radius=1
    g323: Circle CenterX=42.0728 CenterY=-91.7794 CenterZ=0 NormalX=0 NormalY=0 NormalZ=1 AngleXU=0 Radius=1
    g324: BSplineCurve PolesCount=3 KnotsCount=2 Degree=2 IsPeriodic=0
    g325: GeomPoint X=46.0728 Y=-87.7794 Z=0
    g326: GeomPoint X=42.0728 Y=-91.7794 Z=0
    g327: Circle CenterX=2.07281 CenterY=-91.7794 CenterZ=0 NormalX=0 NormalY=0 NormalZ=1 AngleXU=0 Radius=1
    g328: Circle CenterX=-1.92719 CenterY=-91.7794 CenterZ=0 NormalX=0 NormalY=0 NormalZ=1 AngleXU=0 Radius=1
    g329: Circle CenterX=1.57905 CenterY=-89.8542 CenterZ=0 NormalX=0 NormalY=0 NormalZ=1 AngleXU=0 Radius=1
    g330: BSplineCurve PolesCount=3 KnotsCount=2 Degree=2 IsPeriodic=0
    g331: GeomPoint X=2.07281 Y=-91.7794 Z=0
    g332: GeomPoint X=1.57905 Y=-89.8542 Z=0
    g333: LineSegment StartX=2.07281 StartY=-91.7794 StartZ=0 EndX=42.0728 EndY=-91.7794 EndZ=0
    g334: LineSegment StartX=46.0728 StartY=-87.7794 StartZ=0 EndX=46.0728 EndY=-69.424 EndZ=0
    g335: LineSegment StartX=42.5666 StartY=-67.3492 StartZ=0 EndX=1.57905 EndY=-89.8542 EndZ=0
    g336: Circle CenterX=322.073 CenterY=76.4095 CenterZ=0 NormalX=0 NormalY=0 NormalZ=1 AngleXU=0 Radius=4
    g337: BSplineCurve PolesCount=3 KnotsCount=2 Degree=2 IsPeriodic=0
    g338: GeomPoint X=318.073 Y=72.4095 Z=0
    g339: GeomPoint X=322.073 Y=76.4095 Z=0
    g340: Circle CenterX=375.073 CenterY=72.4095 CenterZ=0 NormalX=0 NormalY=0 NormalZ=1 AngleXU=0 Radius=1
    g341: Circle CenterX=375.073 CenterY=76.4095 CenterZ=0 NormalX=0 NormalY=0 NormalZ=1 AngleXU=0 Radius=1
    g342: Circle CenterX=371.073 CenterY=76.4095 CenterZ=0 NormalX=0 NormalY=0 NormalZ=1 AngleXU=0 Radius=1
    g343: BSplineCurve PolesCount=3 KnotsCount=2 Degree=2 IsPeriodic=0
    g344: GeomPoint X=375.073 Y=72.4095 Z=0
    g345: GeomPoint X=371.073 Y=76.4095 Z=0
    g346: LineSegment StartX=322.073 StartY=76.4095 StartZ=0 EndX=371.073 EndY=76.4095 EndZ=0
    g347: LineSegment StartX=318.073 StartY=72.4095 StartZ=0 EndX=318.073 EndY=-47.4823 EndZ=0
    g348: LineSegment StartX=375.073 StartY=72.4095 StartZ=0 EndX=375.073 EndY=-78.7896 EndZ=0
  constraints (576):
    c: Coincident(g0,g2)
    c: Block(g0)
    c: Block(g1)
    c: Vertical(g3)
    c: Vertical(g4)
    c: Block(g4)
    c: Block(g3)
    c: Tangent(g5,g8) = 1.5708
    c: Tangent(g5,g7) = -1.5708
    c: Tangent(g7,g6) = -1.5708
    c: Tangent(g8,g6) = 1.5708
    c: Vertical(g7)
    c: Equal(g5,g6)
    c: Block(g8)
    c: Block(g7)
    c: Tangent(g9,g10) = 1.5708
    c: Tangent(g10,g12) = 1.5708
    c: Equal(g9,g12)
    c: Coincident(g11,g9)
    c: Coincident(g11,g12)
    c: Block(g10)
    c: Block(g11)
    c: Weight(g13) = 1
    c: Equal(g13,g14)
    c: Equal(g13,g15)
    c: InternalAlignment(g13,g16)
    c: InternalAlignment(g14,g16)
    c: InternalAlignment(g15,g16)
    c: InternalAlignment(g17,g16)
    c: InternalAlignment(g18,g16)
    c: Weight(g19) = 1
    c: Equal(g19,g20)
    c: Equal(g19,g21)
    c: InternalAlignment(g19,g22)
    c: InternalAlignment(g20,g22)
    c: InternalAlignment(g21,g22)
    c: InternalAlignment(g23,g22)
    c: InternalAlignment(g24,g22)
    c: Block(g22)
    c: Block(g16)
    c: Weight(g25) = 1
    c: Equal(g25,g26)
    c: Equal(g25,g27)
    c: InternalAlignment(g25,g28)
    c: InternalAlignment(g26,g28)
    c: InternalAlignment(g27,g28)
    c: InternalAlignment(g29,g28)
    c: InternalAlignment(g30,g28)
    c: Weight(g31) = 1
    c: Equal(g31,g32)
    c: Equal(g31,g33)
    c: InternalAlignment(g31,g34)
    c: InternalAlignment(g32,g34)
    c: InternalAlignment(g33,g34)
    c: InternalAlignment(g35,g34)
    c: InternalAlignment(g36,g34)
    c: Block(g34)
    c: Block(g28)
    c: Weight(g37) = 1
    c: Equal(g37,g38)
    c: Equal(g37,g39)
    c: InternalAlignment(g37,g40)
    c: InternalAlignment(g38,g40)
    c: InternalAlignment(g39,g40)
    c: InternalAlignment(g41,g40)
    c: InternalAlignment(g42,g40)
    c: Weight(g43) = 1
    c: Equal(g43,g44)
    c: Equal(g43,g45)
    c: InternalAlignment(g43,g46)
    c: InternalAlignment(g44,g46)
    c: InternalAlignment(g45,g46)
    c: InternalAlignment(g47,g46)
    c: InternalAlignment(g48,g46)
    c: Block(g40)
    c: Block(g46)
    c: Coincident(g49,g4)
    c: Coincident(g49,g3)
    c: Horizontal(g49)
    c: Distance(g49) = 450
    c: Coincident(g50,g4)
    c: Coincident(g50,g3)
    c: Horizontal(g50)
    c: Horizontal(g51)
    c: Coincident(g2,g51)
    c: Block(g51)
    c: Coincident(g1,g51)
    c: Weight(g52) = 1
    c: Equal(g52,g53)
    c: Equal(g52,g54)
    c: InternalAlignment(g52,g55)
    c: InternalAlignment(g53,g55)
    c: InternalAlignment(g54,g55)
    c: InternalAlignment(g56,g55)
    c: InternalAlignment(g57,g55)
    c: Block(g55)
    c: Weight(g58) = 1
    c: Equal(g58,g59)
    c: Equal(g58,g60)
    c: InternalAlignment(g58,g61)
    c: InternalAlignment(g59,g61)
    c: InternalAlignment(g60,g61)
    c: InternalAlignment(g62,g61)
    c: InternalAlignment(g63,g61)
    c: Block(g61)
    c: Weight(g64) = 1
    c: Equal(g64,g65)
    c: Equal(g64,g66)
    c: InternalAlignment(g64,g67)
    c: InternalAlignment(g65,g67)
    c: InternalAlignment(g66,g67)
    c: InternalAlignment(g68,g67)
    c: InternalAlignment(g69,g67)
    c: Block(g67)
    c: Weight(g70) = 1
    c: Equal(g70,g71)
    c: Equal(g70,g72)
    c: InternalAlignment(g70,g73)
    c: InternalAlignment(g71,g73)
    c: InternalAlignment(g72,g73)
    c: InternalAlignment(g74,g73)
    c: InternalAlignment(g75,g73)
    c: Block(g73)
    c: Weight(g76) = 1
    c: Equal(g76,g77)
    c: Equal(g76,g78)
    c: InternalAlignment(g76,g79)
    c: InternalAlignment(g77,g79)
    c: InternalAlignment(g78,g79)
    c: InternalAlignment(g80,g79)
    c: InternalAlignment(g81,g79)
    c: Weight(g82) = 1
    c: Equal(g82,g83)
    c: Equal(g82,g84)
    c: InternalAlignment(g82,g85)
    c: InternalAlignment(g83,g85)
    c: InternalAlignment(g84,g85)
    c: InternalAlignment(g86,g85)
    c: InternalAlignment(g87,g85)
    c: Block(g79)
    c: Block(g85)
    c: Coincident(g88,g79)
    c: Coincident(g88,g85)
    c: Vertical(g88)
    c: Coincident(g89,g79)
    c: Coincident(g89,g61)
    c: Coincident(g90,g61)
    c: Coincident(g90,g85)
    c: Weight(g91) = 1
    c: Equal(g91,g92)
    c: Equal(g91,g93)
    c: InternalAlignment(g91,g94)
    c: InternalAlignment(g92,g94)
    c: InternalAlignment(g93,g94)
    c: InternalAlignment(g95,g94)
    c: InternalAlignment(g96,g94)
    c: Weight(g97) = 1
    c: Equal(g97,g98)
    c: Equal(g97,g99)
    c: InternalAlignment(g97,g100)
    c: InternalAlignment(g98,g100)
    c: InternalAlignment(g99,g100)
    c: InternalAlignment(g101,g100)
    c: InternalAlignment(g102,g100)
    c: Block(g94)
    c: Block(g100)
    c: Coincident(g103,g94)
    c: Coincident(g103,g100)
    c: Vertical(g103)
    c: Coincident(g104,g94)
    c: Coincident(g104,g55)
    c: Coincident(g105,g55)
    c: Coincident(g105,g100)
    c: Weight(g106) = 1
    c: Equal(g106,g107)
    c: Equal(g106,g108)
    c: InternalAlignment(g106,g109)
    c: InternalAlignment(g107,g109)
    c: InternalAlignment(g108,g109)
    c: InternalAlignment(g110,g109)
    c: InternalAlignment(g111,g109)
    c: Weight(g112) = 1
    c: Equal(g112,g113)
    c: Equal(g112,g114)
    c: InternalAlignment(g112,g115)
    c: InternalAlignment(g113,g115)
    c: InternalAlignment(g114,g115)
    c: InternalAlignment(g116,g115)
    c: InternalAlignment(g117,g115)
    c: Block(g109)
    c: Block(g115)
    c: Coincident(g118,g109)
    c: Coincident(g118,g115)
    c: Vertical(g118)
    c: Coincident(g119,g115)
    c: Coincident(g119,g73)
    c: Coincident(g120,g73)
    c: Coincident(g120,g109)
    c: Weight(g121) = 1
    c: Equal(g121,g122)
    c: Equal(g121,g123)
    c: InternalAlignment(g121,g124)
    c: InternalAlignment(g122,g124)
    c: InternalAlignment(g123,g124)
    c: InternalAlignment(g125,g124)
    c: InternalAlignment(g126,g124)
    c: Weight(g127) = 1
    c: Equal(g127,g128)
    c: Equal(g127,g129)
    c: InternalAlignment(g127,g130)
    c: InternalAlignment(g128,g130)
    c: InternalAlignment(g129,g130)
    c: InternalAlignment(g131,g130)
    c: InternalAlignment(g132,g130)
    c: Block(g124)
    c: Block(g130)
    c: Coincident(g133,g124)
    c: Coincident(g133,g130)
    c: Vertical(g133)
    c: Coincident(g134,g130)
    c: Coincident(g134,g67)
    c: Coincident(g135,g67)
    c: Coincident(g135,g124)
    c: Weight(g136) = 1
    c: Equal(g136,g137)
    c: Equal(g136,g138)
    c: InternalAlignment(g136,g139)
    c: InternalAlignment(g137,g139)
    c: InternalAlignment(g138,g139)
    c: InternalAlignment(g140,g139)
    c: InternalAlignment(g141,g139)
    c: Weight(g142) = 1
    c: Equal(g142,g143)
    c: Equal(g142,g144)
    c: InternalAlignment(g142,g145)
    c: InternalAlignment(g143,g145)
    c: InternalAlignment(g144,g145)
    c: InternalAlignment(g146,g145)
    c: InternalAlignment(g147,g145)
    c: Weight(g148) = 1
    c: Equal(g148,g149)
    c: Equal(g148,g150)
    c: InternalAlignment(g148,g151)
    c: InternalAlignment(g149,g151)
    c: InternalAlignment(g150,g151)
    c: InternalAlignment(g152,g151)
    c: InternalAlignment(g153,g151)
    c: Weight(g154) = 1
    c: Equal(g154,g155)
    c: Equal(g154,g156)
    c: InternalAlignment(g154,g157)
    c: InternalAlignment(g155,g157)
    c: InternalAlignment(g156,g157)
    c: InternalAlignment(g158,g157)
    c: InternalAlignment(g159,g157)
    c: Block(g157)
    c: Block(g151)
    c: Block(g145)
    c: Block(g139)
    c: Coincident(g160,g34)
    c: Coincident(g160,g157)
    c: Coincident(g161,g157)
    c: Coincident(g161,g151)
    c: Horizontal(g161)
    c: Coincident(g162,g151)
    c: Coincident(g162,g34)
    c: Vertical(g162)
    c: Coincident(g163,g28)
    c: Coincident(g163,g145)
    c: Vertical(g163)
    c: Coincident(g164,g145)
    c: Coincident(g164,g139)
    c: Horizontal(g164)
    c: Coincident(g165,g139)
    c: Coincident(g165,g28)
    c: Weight(g166) = 1
    c: Equal(g166,g167)
    c: Equal(g166,g168)
    c: InternalAlignment(g166,g169)
    c: InternalAlignment(g167,g169)
    c: InternalAlignment(g168,g169)
    c: InternalAlignment(g170,g169)
    c: InternalAlignment(g171,g169)
    c: Weight(g172) = 1
    c: Equal(g172,g173)
    c: Equal(g172,g174)
    c: InternalAlignment(g172,g175)
    c: InternalAlignment(g173,g175)
    c: InternalAlignment(g174,g175)
    c: InternalAlignment(g176,g175)
    c: InternalAlignment(g177,g175)
    c: Weight(g178) = 1
    c: Equal(g178,g179)
    c: Equal(g178,g180)
    c: InternalAlignment(g178,g181)
    c: InternalAlignment(g179,g181)
    c: InternalAlignment(g180,g181)
    c: InternalAlignment(g182,g181)
    c: InternalAlignment(g183,g181)
    c: Weight(g184) = 1
    c: Equal(g184,g185)
    c: Equal(g184,g186)
    c: InternalAlignment(g184,g187)
    c: InternalAlignment(g185,g187)
    c: InternalAlignment(g186,g187)
    c: InternalAlignment(g188,g187)
    c: InternalAlignment(g189,g187)
    c: Block(g187)
    c: Block(g181)
    c: Block(g175)
    c: Block(g169)
    c: Coincident(g190,g187)
    c: Coincident(g190,g181)
    c: Horizontal(g190)
    c: Coincident(g191,g181)
    c: Coincident(g191,g16)
    c: Vertical(g191)
    c: Coincident(g192,g22)
    c: Coincident(g192,g175)
    c: Vertical(g192)
    c: Coincident(g193,g175)
    c: Coincident(g193,g169)
    c: Horizontal(g193)
    c: Coincident(g194,g169)
    c: Coincident(g194,g22)
    c: Coincident(g195,g16)
    c: Weight(g196) = 1
    c: Equal(g196,g197)
    c: Equal(g196,g198)
    c: InternalAlignment(g196,g199)
    c: InternalAlignment(g197,g199)
    c: InternalAlignment(g198,g199)
    c: InternalAlignment(g200,g199)
    c: InternalAlignment(g201,g199)
    c: Weight(g202) = 1
    c: Equal(g202,g203)
    c: Equal(g202,g204)
    c: InternalAlignment(g202,g205)
    c: InternalAlignment(g203,g205)
    c: InternalAlignment(g204,g205)
    c: InternalAlignment(g206,g205)
    c: InternalAlignment(g207,g205)
    c: Block(g205)
    c: Block(g199)
    c: Coincident(g208,g205)
    c: Coincident(g208,g40)
    c: Coincident(g209,g40)
    c: Coincident(g209,g199)
    c: Coincident(g210,g199)
    c: Coincident(g210,g205)
    c: Vertical(g210)
    c: Weight(g211) = 1
    c: Equal(g211,g212)
    c: Equal(g211,g213)
    c: InternalAlignment(g211,g214)
    c: InternalAlignment(g212,g214)
    c: InternalAlignment(g213,g214)
    c: InternalAlignment(g215,g214)
    c: InternalAlignment(g216,g214)
    c: Weight(g217) = 1
    c: Equal(g217,g218)
    c: Equal(g217,g219)
    c: InternalAlignment(g217,g220)
    c: InternalAlignment(g218,g220)
    c: InternalAlignment(g219,g220)
    c: InternalAlignment(g221,g220)
    c: InternalAlignment(g222,g220)
    c: Block(g220)
    c: Block(g214)
    c: Coincident(g223,g214)
    c: Coincident(g223,g46)
    c: Coincident(g224,g46)
    c: Coincident(g224,g220)
    c: Coincident(g225,g220)
    c: Coincident(g225,g214)
    c: Vertical(g225)
    c: Horizontal(g226)
    c: Block(g226)
    c: Vertical(g227)
    c: Block(g227)
    c: Block(g228)
    c: Weight(g229) = 1
    c: Equal(g229,g230)
    c: Equal(g229,g231)
    c: InternalAlignment(g229,g232)
    c: InternalAlignment(g230,g232)
    c: InternalAlignment(g231,g232)
    c: InternalAlignment(g233,g232)
    c: InternalAlignment(g234,g232)
    c: Weight(g235) = 1
    c: Equal(g235,g236)
    c: Equal(g235,g237)
    c: InternalAlignment(g235,g238)
    c: InternalAlignment(g236,g238)
    c: InternalAlignment(g237,g238)
    c: InternalAlignment(g239,g238)
    c: InternalAlignment(g240,g238)
    c: Weight(g241) = 1
    c: Equal(g241,g242)
    c: Equal(g241,g243)
    c: InternalAlignment(g241,g244)
    c: InternalAlignment(g242,g244)
    c: InternalAlignment(g243,g244)
    c: InternalAlignment(g245,g244)
    c: InternalAlignment(g246,g244)
    c: Weight(g247) = 1
    c: Equal(g247,g248)
    c: Equal(g247,g249)
    c: InternalAlignment(g247,g250)
    c: InternalAlignment(g248,g250)
    c: InternalAlignment(g249,g250)
    c: InternalAlignment(g251,g250)
    c: InternalAlignment(g252,g250)
    c: Block(g232)
    c: Block(g238)
    c: Block(g244)
    c: Block(g250)
    c: Coincident(g253,g238)
    c: Coincident(g253,g232)
    c: Horizontal(g253)
    c: Block(g195)
    c: Weight(g254) = 1
    c: Equal(g254,g255)
    c: Equal(g254,g256)
    c: InternalAlignment(g254,g257)
    c: InternalAlignment(g255,g257)
    c: InternalAlignment(g256,g257)
    c: InternalAlignment(g258,g257)
    c: InternalAlignment(g259,g257)
    c: Weight(g260) = 1
    c: Equal(g260,g261)
    c: Equal(g260,g262)
    c: InternalAlignment(g260,g263)
    c: InternalAlignment(g261,g263)
    c: InternalAlignment(g262,g263)
    c: InternalAlignment(g264,g263)
    c: InternalAlignment(g265,g263)
    c: Block(g257)
    c: Block(g263)
    c: Coincident(g266,g257)
    c: Coincident(g266,g263)
    c: Weight(g267) = 1
    c: Equal(g267,g268)
    c: Equal(g267,g269)
    c: InternalAlignment(g267,g270)
    c: InternalAlignment(g268,g270)
    c: InternalAlignment(g269,g270)
    c: InternalAlignment(g271,g270)
    c: InternalAlignment(g272,g270)
    c: Weight(g273) = 1
    c: Equal(g273,g274)
    c: Equal(g273,g275)
    c: InternalAlignment(g273,g276)
    c: InternalAlignment(g274,g276)
    c: InternalAlignment(g275,g276)
    c: InternalAlignment(g277,g276)
    c: InternalAlignment(g278,g276)
    c: Weight(g279) = 1
    c: Equal(g279,g280)
    c: Equal(g279,g281)
    c: InternalAlignment(g279,g282)
    c: InternalAlignment(g280,g282)
    c: InternalAlignment(g281,g282)
    c: InternalAlignment(g283,g282)
    c: InternalAlignment(g284,g282)
    c: Block(g282)
    c: Block(g276)
    c: Block(g270)
    c: Coincident(g285,g276)
    c: Coincident(g285,g270)
    c: Coincident(g286,g270)
    c: Coincident(g286,g282)
    c: Vertical(g286)
    c: Coincident(g287,g282)
    c: Coincident(g287,g276)
    c: Horizontal(g287)
    c: Weight(g288) = 1
    c: Equal(g288,g289)
    c: InternalAlignment(g288,g290)
    c: InternalAlignment(g289,g290)
    c: InternalAlignment(g291,g290)
    c: InternalAlignment(g292,g290)
    c: Weight(g293) = 1
    c: Equal(g293,g294)
    c: Equal(g293,g295)
    c: InternalAlignment(g293,g296)
    c: InternalAlignment(g294,g296)
    c: InternalAlignment(g295,g296)
    c: InternalAlignment(g297,g296)
    c: InternalAlignment(g298,g296)
    c: Weight(g299) = 1
    c: Equal(g299,g300)
    c: Equal(g299,g301)
    c: InternalAlignment(g299,g302)
    c: InternalAlignment(g300,g302)
    c: InternalAlignment(g301,g302)
    c: InternalAlignment(g303,g302)
    c: InternalAlignment(g304,g302)
    c: Equal(g305,g306)
    c: Equal(g305,g307)
    c: InternalAlignment(g305,g308)
    c: InternalAlignment(g306,g308)
    c: InternalAlignment(g307,g308)
    c: InternalAlignment(g309,g308)
    c: InternalAlignment(g310,g308)
    c: Block(g296)
    c: Block(g302)
    c: Block(g308)
    c: Block(g290)
    c: Coincident(g311,g290)
    c: Coincident(g311,g296)
    c: Horizontal(g311)
    c: Coincident(g312,g296)
    c: Coincident(g312,g302)
    c: Vertical(g312)
    c: Coincident(g313,g302)
    c: Coincident(g313,g308)
    c: Horizontal(g313)
    c: Coincident(g314,g308)
    c: Coincident(g314,g290)
    c: Weight(g315) = 1
    c: Equal(g315,g316)
    c: Equal(g315,g317)
    c: InternalAlignment(g315,g318)
    c: InternalAlignment(g316,g318)
    c: InternalAlignment(g317,g318)
    c: InternalAlignment(g319,g318)
    c: InternalAlignment(g320,g318)
    c: Weight(g321) = 1
    c: Equal(g321,g322)
    c: Equal(g321,g323)
    c: InternalAlignment(g321,g324)
    c: InternalAlignment(g322,g324)
    c: InternalAlignment(g323,g324)
    c: InternalAlignment(g325,g324)
    c: InternalAlignment(g326,g324)
    c: Weight(g327) = 1
    c: Equal(g327,g328)
    c: Equal(g327,g329)
    c: InternalAlignment(g327,g330)
    c: InternalAlignment(g328,g330)
    c: InternalAlignment(g329,g330)
    c: InternalAlignment(g331,g330)
    c: InternalAlignment(g332,g330)
    c: Block(g330)
    c: Block(g324)
    c: Block(g318)
    c: Coincident(g333,g330)
    c: Coincident(g333,g324)
    c: Horizontal(g333)
    c: Coincident(g334,g324)
    c: Coincident(g334,g318)
    c: Vertical(g334)
    c: Coincident(g335,g318)
    c: Coincident(g335,g330)
    c: InternalAlignment(g336,g337)
    c: InternalAlignment(g338,g337)
    c: InternalAlignment(g339,g337)
    c: Block(g337)
    c: Equal(g340,g341)
    c: Equal(g340,g342)
    c: InternalAlignment(g340,g343)
    c: InternalAlignment(g341,g343)
    c: InternalAlignment(g342,g343)
    c: InternalAlignment(g344,g343)
    c: InternalAlignment(g345,g343)
    c: Block(g343)
    c: Coincident(g346,g337)
    c: Horizontal(g346)
    c: Block(g346)
    c: Coincident(g347,g337)
    c: Coincident(g347,g263)
    c: Vertical(g347)
    c: Coincident(g348,g343)
    c: Coincident(g348,g257)
    c: Vertical(g348)
FEATURE [Sketcher::SketchObject] Sketch001
  FullyConstrained = true
  MapMode = 4
  Placement = pos=(0,0,0) rot=(0.57735,0.57735,0.57735;2.0944rad)
  Support = -> [Sketch]
  sketch-geometry (46):
    g0: BSplineCurve PolesCount=3 KnotsCount=2 Degree=2 IsPeriodic=0
    g1: ArcOfCircle CenterX=73.1223 CenterY=-32.291 CenterZ=0 NormalX=0 NormalY=0 NormalZ=1 AngleXU=0 Radius=13 StartAngle=5.92268 EndAngle=9.06428
    g2: ArcOfCircle CenterX=66.7816 CenterY=-49.1439 CenterZ=0 NormalX=0 NormalY=0 NormalZ=1 AngleXU=0 Radius=13 StartAngle=2.78068 EndAngle=5.92131
    g3: ArcOfCircle CenterX=55.9263 CenterY=-78.1807 CenterZ=0 NormalX=0 NormalY=0 NormalZ=1 AngleXU=0 Radius=13 StartAngle=5.92268 EndAngle=9.06428
    g4: ArcOfCircle CenterX=49.5884 CenterY=-95.0342 CenterZ=0 NormalX=0 NormalY=0 NormalZ=1 AngleXU=0 Radius=13 StartAngle=2.78068 EndAngle=5.92131
    g5: ArcOfCircle CenterX=38.7206 CenterY=-124.067 CenterZ=0 NormalX=0 NormalY=0 NormalZ=1 AngleXU=0 Radius=13 StartAngle=5.92268 EndAngle=9.06428
    g6: ArcOfCircle CenterX=32.3875 CenterY=-140.92 CenterZ=0 NormalX=0 NormalY=0 NormalZ=1 AngleXU=0 Radius=13 StartAngle=2.78068 EndAngle=5.92131
    g7: ArcOfCircle CenterX=21.4715 CenterY=-169.934 CenterZ=0 NormalX=0 NormalY=0 NormalZ=1 AngleXU=0 Radius=13 StartAngle=5.92268 EndAngle=9.06428
    g8: ArcOfCircle CenterX=15.1336 CenterY=-186.787 CenterZ=0 NormalX=0 NormalY=0 NormalZ=1 AngleXU=0 Radius=13 StartAngle=2.78068 EndAngle=5.92131
    g9-g12: Circle x4 (B-spline internal-alignment scaffolding for g13; pole/knot coordinates omitted)
    g13: BSplineCurve PolesCount=4 KnotsCount=2 Degree=3 IsPeriodic=0
    g14: GeomPoint X=28.8094 Y=-19.0875 Z=0
    g15: GeomPoint X=47.0443 Y=-50.4712 Z=0
    g16: Circle CenterX=53.5586 CenterY=-23.2695 CenterZ=0 NormalX=0 NormalY=0 NormalZ=1 AngleXU=0 Radius=3.24518
    g17: Circle CenterX=-195.441 CenterY=-127.082 CenterZ=0 NormalX=0 NormalY=0 NormalZ=1 AngleXU=0 Radius=1
    g18: Circle CenterX=-8.24091 CenterY=-197.481 CenterZ=0 NormalX=0 NormalY=0 NormalZ=1 AngleXU=0 Radius=1
    g19: Circle CenterX=12.8789 CenterY=-141.321 CenterZ=0 NormalX=0 NormalY=0 NormalZ=1 AngleXU=0 Radius=1
    g20: BSplineCurve PolesCount=3 KnotsCount=2 Degree=2 IsPeriodic=0
    g21: GeomPoint X=-195.441 Y=-127.082 Z=0
    g22: GeomPoint X=12.8789 Y=-141.321 Z=0
    g23: Circle CenterX=-12.8016 CenterY=-179.036 CenterZ=0 NormalX=0 NormalY=0 NormalZ=1 AngleXU=0 Radius=10.5072
    g24: Circle CenterX=0.933922 CenterY=-166.43 CenterZ=0 NormalX=0 NormalY=0 NormalZ=1 AngleXU=0 Radius=3.26661
    g25: Circle CenterX=-33.5518 CenterY=-176.44 CenterZ=0 NormalX=0 NormalY=0 NormalZ=1 AngleXU=0 Radius=5.64388
    g26: Circle CenterX=-47.2366 CenterY=-173.859 CenterZ=0 NormalX=0 NormalY=0 NormalZ=1 AngleXU=0 Radius=3.01653
    g27: Circle CenterX=-56.2595 CenterY=-171.456 CenterZ=0 NormalX=0 NormalY=0 NormalZ=1 AngleXU=0 Radius=2.12826
    g28: ArcOfCircle CenterX=51.2151 CenterY=-198.473 CenterZ=0 NormalX=0 NormalY=0 NormalZ=1 AngleXU=0 Radius=20 StartAngle=2.78189 EndAngle=4.35269
    g29: LineSegment StartX=32.4951 StartY=-191.433 StartZ=0 EndX=94.6578 EndY=-26.1352 EndZ=0
    g30: LineSegment StartX=43.1192 StartY=-220.001 StartZ=0 EndX=-196.497 EndY=-129.89 EndZ=0
    g31: LineSegment StartX=43.1192 StartY=-220.001 StartZ=0 EndX=44.1752 EndY=-217.193 EndZ=0
    g32: LineSegment StartX=117.223 StartY=-19.0875 StartZ=0 EndX=117.223 EndY=-16.0875 EndZ=0
    g33: LineSegment StartX=117.223 StartY=-16.0875 StartZ=0 EndX=17.2232 EndY=-16.0875 EndZ=0
    g34: LineSegment StartX=17.2232 StartY=-16.0875 StartZ=0 EndX=17.2232 EndY=-19.0875 EndZ=0
    g35: LineSegment StartX=28.8094 StartY=-19.0875 StartZ=0 EndX=17.2232 EndY=-19.0875 EndZ=0
    g36: LineSegment StartX=47.0443 StartY=-50.4712 StartZ=0 EndX=12.8789 EndY=-141.321 EndZ=0
    g37: LineSegment StartX=-195.441 StartY=-127.082 StartZ=0 EndX=-196.497 EndY=-129.89 EndZ=0
    g38: LineSegment StartX=85.2866 StartY=-36.8766 StartZ=0 EndX=78.9396 EndY=-53.7463 EndZ=0
    g39: LineSegment StartX=60.9579 StartY=-27.7053 StartZ=0 EndX=54.6191 EndY=-44.5532 EndZ=0
    g40: LineSegment StartX=68.0907 StartY=-82.7664 StartZ=0 EndX=61.7465 EndY=-99.6365 EndZ=0
    g41: LineSegment StartX=43.7619 StartY=-73.595 StartZ=0 EndX=37.426 EndY=-90.4435 EndZ=0
    g42: LineSegment StartX=50.885 StartY=-128.652 StartZ=0 EndX=44.5456 EndY=-145.522 EndZ=0
    g43: LineSegment StartX=26.5562 StartY=-119.481 StartZ=0 EndX=20.2251 EndY=-136.329 EndZ=0
    g44: LineSegment StartX=9.3071 StartY=-165.349 StartZ=0 EndX=2.97115 EndY=-182.197 EndZ=0
    g45: LineSegment StartX=33.6358 StartY=-174.52 StartZ=0 EndX=27.2917 EndY=-191.39 EndZ=0
  constraints (71):
    c: Block(g0)
    c: Block(g1)
    c: Block(g2)
    c: Block(g4)
    c: Block(g3)
    c: Block(g6)
    c: Block(g5)
    c: Block(g8)
    c: Block(g7)
    c: Weight(g9) = 1
    c: Equal(g9,g10)
    c: Equal(g9,g11)
    c: Equal(g9,g12)
    c: InternalAlignment(g9-g12 -> g13) x4
    c: InternalAlignment(g14,g13)
    c: InternalAlignment(g15,g13)
    c: Block(g16)
    c: Weight(g17) = 1
    c: Equal(g17,g18)
    c: Equal(g17,g19)
    c: InternalAlignment(g17,g20)
    c: InternalAlignment(g18,g20)
    c: InternalAlignment(g19,g20)
    c: InternalAlignment(g21,g20)
    c: InternalAlignment(g22,g20)
    c: Block(g20)
    c: Block(g23)
    c: Block(g24)
    c: Block(g25)
    c: Block(g26)
    c: Block(g27)
    c: Block(g28)
    c: Coincident(g29,g28)
    c: Coincident(g29,g0)
    c: Block(g13)
    c: Coincident(g31,g30)
    c: Coincident(g31,g28)
    c: Block(g31)
    c: Coincident(g32,g0)
    c: Vertical(g32)
    c: Coincident(g33,g32)
    c: Horizontal(g33)
    c: Coincident(g34,g33)
    c: Vertical(g34)
    c: Block(g33)
    c: Coincident(g35,g13)
    c: Coincident(g35,g34)
    c: Horizontal(g35)
    c: Coincident(g36,g13)
    c: Coincident(g36,g20)
    c: Coincident(g37,g20)
    c: Coincident(g37,g30)
    c: Block(g30)
    c: Coincident(g38,g1)
    c: Coincident(g38,g2)
    c: Coincident(g39,g1)
    c: Coincident(g39,g2)
    c: Coincident(g40,g3)
    c: Coincident(g40,g4)
    c: Coincident(g41,g3)
    c: Coincident(g41,g4)
    c: Coincident(g42,g5)
    c: Coincident(g42,g6)
    c: Coincident(g43,g5)
    c: Coincident(g43,g6)
    c: Coincident(g44,g7)
    c: Coincident(g44,g8)
    c: Coincident(g45,g7)
    c: Coincident(g45,g8)
    c: Distance(g30) = 256
    c: Distance(g33) = 100
FEATURE [Part::Extrusion] Extrude002
  Base = -> Sketch001
  Dir = (1,0,0)
  DirMode = 2
  FaceMakerClass = Part::FaceMakerBullseye
  LengthFwd = 8
  LengthRev = 0
  Solid = true
  Symmetric = false
FEATURE [Sketcher::SketchObject] Sketch002
  FullyConstrained = true
  sketch-geometry (20):
    g0: LineSegment StartX=-2.77179 StartY=-200.304 StartZ=0 EndX=5.22821 EndY=-200.304 EndZ=0
    g1: LineSegment StartX=5.22821 StartY=-200.304 StartZ=0 EndX=5.22821 EndY=-197.304 EndZ=0
    g2: LineSegment StartX=-2.77179 StartY=-200.304 StartZ=0 EndX=-2.77179 EndY=-197.304 EndZ=0
    g3: LineSegment StartX=5.22821 StartY=-197.304 StartZ=0 EndX=8.22821 EndY=-197.304 EndZ=0
    g4: LineSegment StartX=-2.77179 StartY=-197.304 StartZ=0 EndX=-5.77179 EndY=-197.304 EndZ=0
    g5: LineSegment StartX=19.2282 StartY=-203.304 StartZ=0 EndX=19.2282 EndY=-206.304 EndZ=0
    g6: LineSegment StartX=-16.7718 StartY=-203.304 StartZ=0 EndX=-16.7718 EndY=-206.304 EndZ=0
    g7: LineSegment StartX=-16.7718 StartY=-206.304 StartZ=0 EndX=19.2282 EndY=-206.304 EndZ=0
    g8: Circle CenterX=-16.7718 CenterY=-203.304 CenterZ=0 NormalX=0 NormalY=0 NormalZ=1 AngleXU=0 Radius=1
    g9: Circle CenterX=-5.77179 CenterY=-203.304 CenterZ=0 NormalX=0 NormalY=0 NormalZ=1 AngleXU=0 Radius=1
    g10: Circle CenterX=-5.77179 CenterY=-197.304 CenterZ=0 NormalX=0 NormalY=0 NormalZ=1 AngleXU=0 Radius=1
    g11: BSplineCurve PolesCount=3 KnotsCount=2 Degree=2 IsPeriodic=0
    g12: GeomPoint X=-16.7718 Y=-203.304 Z=0
    g13: GeomPoint X=-5.77179 Y=-197.304 Z=0
    g14: Circle CenterX=19.2282 CenterY=-203.304 CenterZ=0 NormalX=0 NormalY=0 NormalZ=1 AngleXU=0 Radius=1
    g15: Circle CenterX=8.22821 CenterY=-203.304 CenterZ=0 NormalX=0 NormalY=0 NormalZ=1 AngleXU=0 Radius=1
    g16: Circle CenterX=8.22821 CenterY=-197.304 CenterZ=0 NormalX=0 NormalY=0 NormalZ=1 AngleXU=0 Radius=1
    g17: BSplineCurve PolesCount=3 KnotsCount=2 Degree=2 IsPeriodic=0
    g18: GeomPoint X=19.2282 Y=-203.304 Z=0
    g19: GeomPoint X=8.22821 Y=-197.304 Z=0
  constraints (41):
    c: Horizontal(g0)
    c: Distance(g0) = 8
    c: Coincident(g1,g0)
    c: Vertical(g1)
    c: Distance(g1) = 3
    c: Coincident(g2,g0)
    c: Vertical(g2)
    c: Distance(g2) = 3
    c: Coincident(g3,g1)
    c: Horizontal(g3)
    c: Distance(g3) = 3
    c: Coincident(g4,g2)
    c: Horizontal(g4)
    c: Distance(g4) = 3
    c: Vertical(g5)
    c: Vertical(g6)
    c: Coincident(g7,g6)
    c: Coincident(g7,g5)
    c: Weight(g8) = 1
    c: Equal(g8,g9)
    c: Equal(g8,g10)
    c: Coincident(g11,g4)
    c: InternalAlignment(g8,g11)
    c: InternalAlignment(g9,g11)
    c: InternalAlignment(g10,g11)
    c: InternalAlignment(g12,g11)
    c: InternalAlignment(g13,g11)
    c: Coincident(g17,g5)
    c: Weight(g14) = 1
    c: Equal(g14,g15)
    c: Equal(g14,g16)
    c: Coincident(g17,g3)
    c: InternalAlignment(g14,g17)
    c: InternalAlignment(g15,g17)
    c: InternalAlignment(g16,g17)
    c: InternalAlignment(g18,g17)
    c: InternalAlignment(g19,g17)
    c: Block(g7)
    c: Block(g17)
    c: Block(g11)
    c: Block(g6)
FEATURE [Part::Extrusion] Extrude003
  Base = -> Sketch002
  Dir = (0,0,1)
  DirMode = 2
  FaceMakerClass = Part::FaceMakerBullseye
  LengthFwd = 260
  LengthRev = 0
  Solid = true
  Symmetric = false
FEATURE [Part::Extrusion] Extrude
  Base = -> Sketch
  Dir = (0,0,1)
  DirMode = 2
  FaceMakerClass = Part::FaceMakerBullseye
  LengthFwd = 14
  LengthRev = 0
  Solid = true
  Symmetric = false
